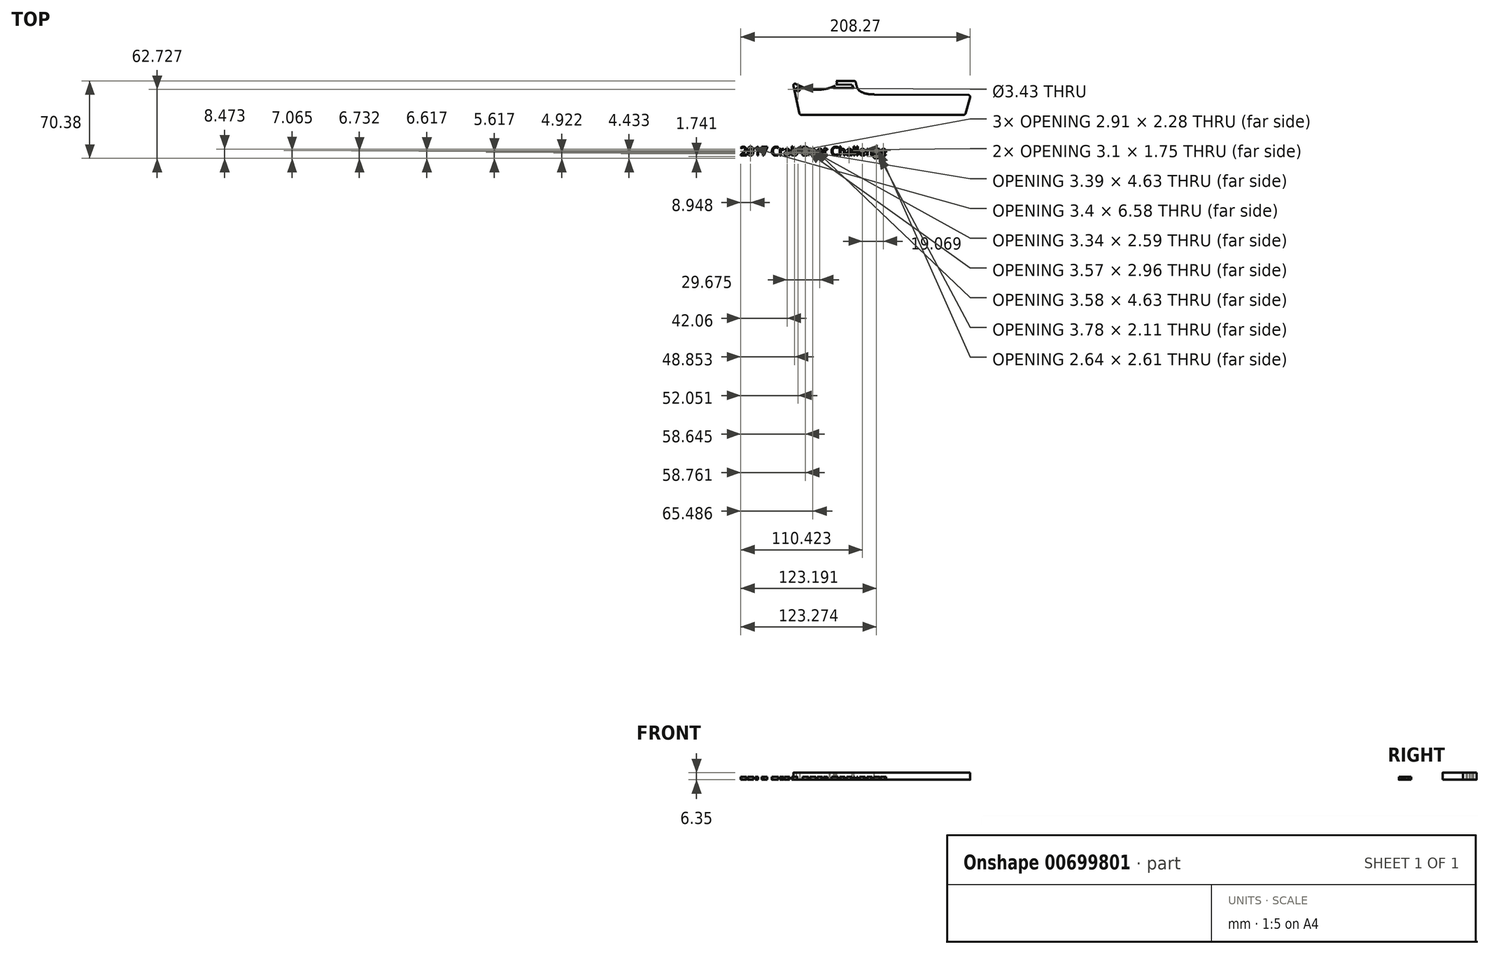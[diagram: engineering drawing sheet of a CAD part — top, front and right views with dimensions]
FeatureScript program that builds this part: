
annotation { "Feature Type Name" : "Feature", "Feature Type Description" : "" }
export const myFeature = defineFeature(function(context is Context, id is Id, definition is map)
    precondition{}
    {
        {
            var Q0;
            Q0=qCreatedBy(makeId("Top.planeOp"),FACE);
            var sketch = newSketch(context, id + "F0", { "sketchPlane" : qUnion([Q0])});
            skLineSegment(sketch, "E0", {"start": v(-84.93, 14.88) * mm, "end": v(-79.38, -10.13) * mm});
            skLineSegment(sketch, "E1", {"start": v(-77.83, -11.38) * mm, "end": v(69.73, -11.38) * mm});
            skLineSegment(sketch, "E2", {"start": v(-29.93, 19.42) * mm, "end": v(-53.77, 19.42) * mm});
            skLineSegment(sketch, "E3", {"start": v(-55.2, 17.15) * mm, "end": v(-54.94, 16.58) * mm});
            skLineSegment(sketch, "E4", {"start": v(-54.94, 16.58) * mm, "end": v(-57.7, 12.86) * mm});
            skLineSegment(sketch, "E5", {"start": v(-57.7, 12.86) * mm, "end": v(-62.45, 12.86) * mm});
            skLineSegment(sketch, "E6", {"start": v(-63.96, 11.78) * mm, "end": v(-64.12, 11.3) * mm});
            skLineSegment(sketch, "E7", {"start": v(-46.82, 16.06) * mm, "end": v(-48.57, 12.91) * mm});
            skLineSegment(sketch, "E8", {"start": v(-48.57, 12.91) * mm, "end": v(-30.25, 13.01) * mm});
            skLineSegment(sketch, "E9", {"start": v(-30.25, 13.01) * mm, "end": v(-31.87, 16) * mm});
            skLineSegment(sketch, "E10", {"start": v(-31.87, 16) * mm, "end": v(-46.82, 16.06) * mm});
            skLineSegment(sketch, "E11", {"start": v(-12.87, 7.14) * mm, "end": v(73.94, 6.6) * mm});
            skFitSpline(sketch, "E12", {"points": [v(-28.7, 19.42) * mm, v(-24.4, 10.07) * mm, v(-13.1, 10.5) * mm], "startDerivative": vector(6.33, -23.36) * mm, "endDerivative": vector(13.02, 12.63) * mm});
            skFitSpline(sketch, "E13", {"points": [v(-24.4, 10.07) * mm, v(-12.87, 7.14) * mm, v(9.04, 10.07) * mm], "startDerivative": vector(24.02, -14.85) * mm, "endDerivative": vector(42.16, 10.48) * mm});
            skFitSpline(sketch, "E14", {"points": [v(-85.67, 18.21) * mm, v(-64.12, 11.3) * mm, v(-45.47, 17.35) * mm, v(-67.3, 29.92) * mm], "startDerivative": vector(57.78, -30.56) * mm, "endDerivative": vector(-95.71, 37.44) * mm});
            skLineSegment(sketch, "E15", {"start": v(-51.94, 12.9) * mm, "end": v(-54.94, 12.88) * mm});
            skLineSegment(sketch, "E16", {"start": v(-54.94, 12.88) * mm, "end": v(-52.32, 16.38) * mm});
            skLineSegment(sketch, "E17", {"start": v(-52.32, 16.38) * mm, "end": v(-50.05, 16.29) * mm});
            skLineSegment(sketch, "E18", {"start": v(-50.05, 16.29) * mm, "end": v(-51.94, 12.9) * mm});
            skArc(sketch, "E19.filletArc", {"start": v(-82.66, 16.64) * mm, "mid": v(-84.35, 16.48) * mm, "end": v(-84.93, 14.88) * mm});
            skArc(sketch, "E20.filletArc", {"start": v(-28.39, 18.2) * mm, "mid": v(-28.95, 19.08) * mm, "end": v(-29.93, 19.42) * mm});
            skPoint(sketch, "E21.visualSharp", {"position": v(-79.1, -11.38) * mm});
            skArc(sketch, "E21.filletArc", {"start": v(-79.38, -10.13) * mm, "mid": v(-78.82, -11.03) * mm, "end": v(-77.83, -11.38) * mm});
            skPoint(sketch, "E22.visualSharp", {"position": v(-63.6, 12.86) * mm});
            skArc(sketch, "E22.filletArc", {"start": v(-62.45, 12.86) * mm, "mid": v(-63.38, 12.56) * mm, "end": v(-63.96, 11.78) * mm});
            skPoint(sketch, "E23.visualSharp", {"position": v(-56.29, 19.42) * mm});
            skArc(sketch, "E23.filletArc", {"start": v(-53.77, 19.42) * mm, "mid": v(-55.12, 18.68) * mm, "end": v(-55.2, 17.15) * mm});
            skCircle(sketch, "E24", {"center": v(-80.7, 11.77) * mm, "radius": 1.71 * mm});
            skLineSegment(sketch, "E25", {"start": v(71.25, -10.22) * mm, "end": v(75.46, 4.58) * mm});
            skPoint(sketch, "E26.visualSharp", {"position": v(76.03, 6.58) * mm});
            skArc(sketch, "E26.filletArc", {"start": v(75.46, 4.58) * mm, "mid": v(75.2, 5.96) * mm, "end": v(73.94, 6.6) * mm});
            skPoint(sketch, "E27.visualSharp", {"position": v(70.93, -11.38) * mm});
            skArc(sketch, "E27.filletArc", {"start": v(69.73, -11.38) * mm, "mid": v(70.68, -11.06) * mm, "end": v(71.25, -10.22) * mm});
            skSolve(sketch);
        }
        {
            var Q0;
            Q0=qCreatedBy(makeId("Top.planeOp"),FACE);
            var sketch = newSketch(context, id + "F1", { "sketchPlane" : qUnion([Q0])});
            skText(sketch, "E28", { "text": "2017 Crab Boat Challenge", "fontName": "OpenSans-Regular.ttf"});
            const initialGuessF1  = {"E28": [-0.13329, -0.0483, 1, 0, 0.00797]};
            skSetInitialGuess(sketch, initialGuessF1);
            skSolve(sketch);
        }
        {
            var Q0;
            Q0=makeQuery(id+"F0.imprint","IMPRINT",FACE,{"disambiguationData":[TD([[makeQuery(id+"F0.imprint","IMPRINT",EDGE,{"derivedFrom":sQuery(id+"F0.wireOp",EDGE,"E0")}),1.0]])]});
            extrude(context, id + "F2", {"entities" : qUnion([Q0]), "depth" : 6.35 * mm, "offsetDistance" : 25.4 * mm});
        }
        {
            var Q0;
            Q0 = qSketchRegion(id + "F1", true);
            extrude(context, id + "F3", {"entities" : qUnion([Q0]), "operationType" : NewBodyOperationType.ADD, "depth" : 2.54 * mm, "offsetDistance" : 25.4 * mm});
        }
    });
